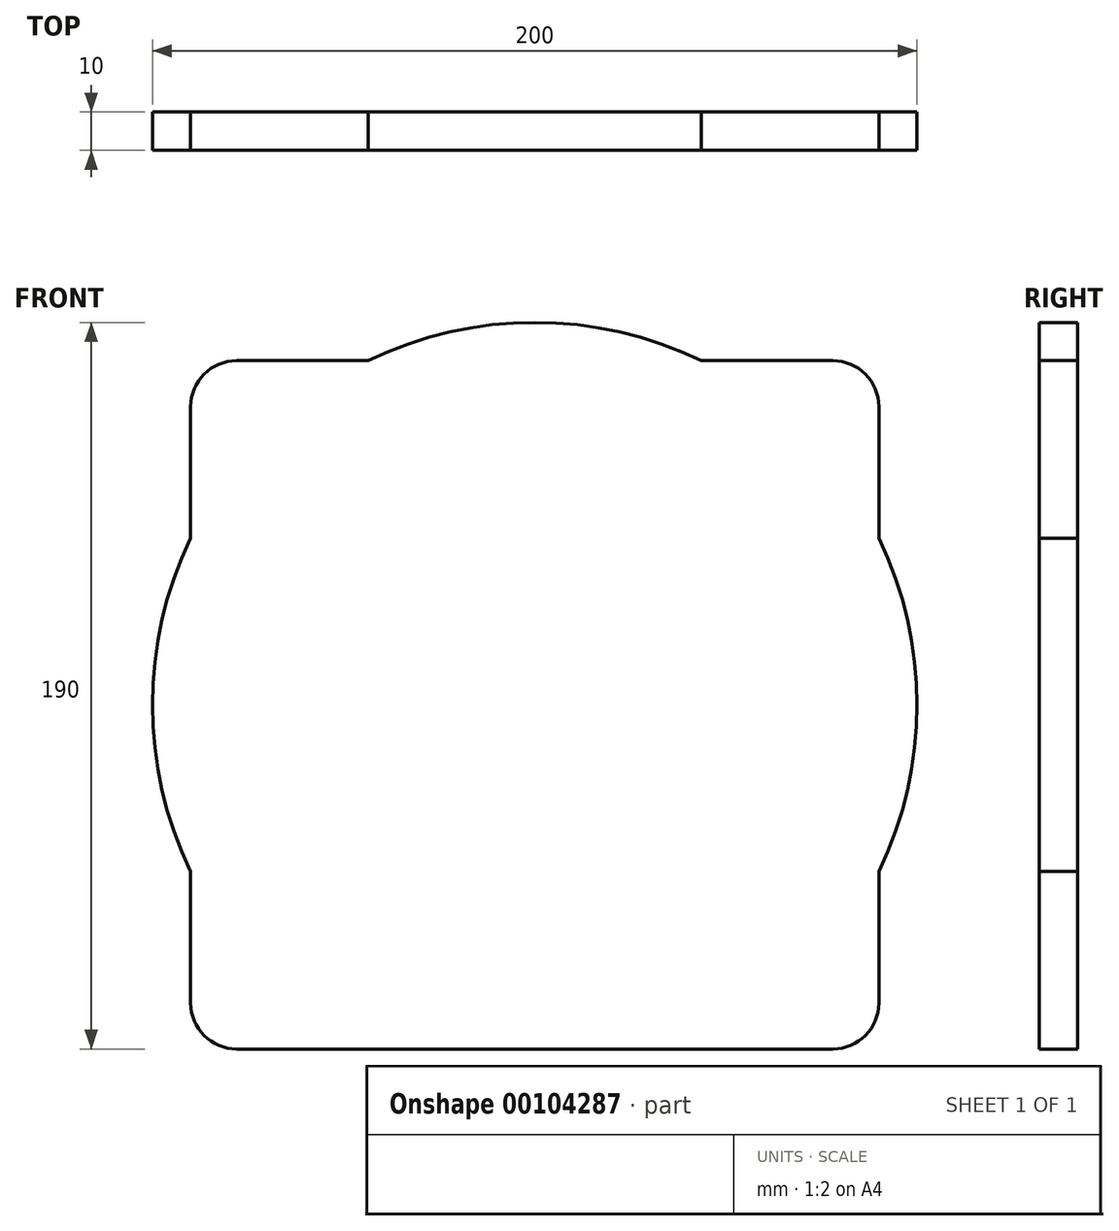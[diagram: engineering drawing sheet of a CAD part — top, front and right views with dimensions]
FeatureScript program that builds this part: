
annotation { "Feature Type Name" : "Feature", "Feature Type Description" : "" }
export const myFeature = defineFeature(function(context is Context, id is Id, definition is map)
    precondition{}
    {
        {
            var Q0;
            Q0=qCreatedBy(makeId("Front.planeOp"),FACE);
            var sketch = newSketch(context, id + "F0", { "sketchPlane" : qUnion([Q0])});
            skCircle(sketch, "E0", {"center": v(0, 0) * mm, "radius": 100 * mm});
            skLineSegment(sketch, "E1.bottom", {"start": v(78, 90) * mm, "end": v(-78, 90) * mm});
            skLineSegment(sketch, "E1.top", {"start": v(78, -90) * mm, "end": v(-78, -90) * mm});
            skLineSegment(sketch, "E1.left", {"start": v(90, 78) * mm, "end": v(90, -78) * mm});
            skLineSegment(sketch, "E1.right", {"start": v(-90, 78) * mm, "end": v(-90, -78) * mm});
            skPoint(sketch, "E2.visualSharp", {"position": v(-90, 90) * mm});
            skArc(sketch, "E2.filletArc", {"start": v(-78, 90) * mm, "mid": v(-86.49, 86.49) * mm, "end": v(-90, 78) * mm});
            skPoint(sketch, "E3.visualSharp", {"position": v(90, 90) * mm});
            skArc(sketch, "E3.filletArc", {"start": v(90, 78) * mm, "mid": v(86.49, 86.49) * mm, "end": v(78, 90) * mm});
            skPoint(sketch, "E4.visualSharp", {"position": v(90, -90) * mm});
            skArc(sketch, "E4.filletArc", {"start": v(78, -90) * mm, "mid": v(86.49, -86.49) * mm, "end": v(90, -78) * mm});
            skPoint(sketch, "E5.visualSharp", {"position": v(-90, -90) * mm});
            skArc(sketch, "E5.filletArc", {"start": v(-90, -78) * mm, "mid": v(-86.49, -86.49) * mm, "end": v(-78, -90) * mm});
            skSolve(sketch);
        }
        {
            var Q0;
            {var subQ5=sQuery(id+"F0.wireOp",EDGE,"E2.filletArc");Q0=makeQuery(id+"F0.imprint","IMPRINT",FACE,{"disambiguationData":[TD([[makeQuery(id+"F0.imprint","IMPRINT",EDGE,{"derivedFrom":subQ5}),1.0]])]});}
            var Q1;
            {var subQ0=sQuery(id+"F0.wireOp",EDGE,"E1.bottom");var subQ1=sQuery(id+"F0.wireOp",EDGE,"E0");var subQ2=makeQuery(id+"F0.imprint","INTERSECT",VERTEX,{"disambiguationData":[OD(0.0)],"derivedFrom":[subQ1,subQ0]});Q1=makeQuery(id+"F0.imprint","IMPRINT",FACE,{"disambiguationData":[TD([[makeQuery(id+"F0.imprint","IMPRINT",EDGE,{"disambiguationData":[TD([[subQ2,-1.0]])],"derivedFrom":subQ1}),1.0]])]});}
            var Q2;
            {var subQ5=sQuery(id+"F0.wireOp",EDGE,"E3.filletArc");Q2=makeQuery(id+"F0.imprint","IMPRINT",FACE,{"disambiguationData":[TD([[makeQuery(id+"F0.imprint","IMPRINT",EDGE,{"derivedFrom":subQ5}),1.0]])]});}
            var Q3;
            {var subQ5=sQuery(id+"F0.wireOp",EDGE,"E4.filletArc");Q3=makeQuery(id+"F0.imprint","IMPRINT",FACE,{"disambiguationData":[TD([[makeQuery(id+"F0.imprint","IMPRINT",EDGE,{"derivedFrom":subQ5}),1.0]])]});}
            var Q4;
            {var subQ5=sQuery(id+"F0.wireOp",EDGE,"E5.filletArc");Q4=makeQuery(id+"F0.imprint","IMPRINT",FACE,{"disambiguationData":[TD([[makeQuery(id+"F0.imprint","IMPRINT",EDGE,{"derivedFrom":subQ5}),1.0]])]});}
            var Q5;
            {var subQ1=sQuery(id+"F0.wireOp",EDGE,"E0");var subQ8=sQuery(id+"F0.wireOp",EDGE,"E1.bottom");var subQ11=makeQuery(id+"F0.imprint","INTERSECT",VERTEX,{"disambiguationData":[OD(0.0)],"derivedFrom":[subQ1,subQ8]});Q5=makeQuery(id+"F0.imprint","IMPRINT",FACE,{"disambiguationData":[TD([[makeQuery(id+"F0.imprint","IMPRINT",EDGE,{"disambiguationData":[TD([[subQ11,1.0]])],"derivedFrom":subQ1}),1.0]])]});}
            var Q6;
            {var subQ0=sQuery(id+"F0.wireOp",EDGE,"E1.right");var subQ1=sQuery(id+"F0.wireOp",EDGE,"E0");var subQ2=makeQuery(id+"F0.imprint","INTERSECT",VERTEX,{"disambiguationData":[OD(0.0)],"derivedFrom":[subQ1,subQ0]});Q6=makeQuery(id+"F0.imprint","IMPRINT",FACE,{"disambiguationData":[TD([[makeQuery(id+"F0.imprint","IMPRINT",EDGE,{"disambiguationData":[TD([[subQ2,-1.0]])],"derivedFrom":subQ1}),1.0]])]});}
            var Q7;
            {var subQ0=sQuery(id+"F0.wireOp",EDGE,"E1.top");var subQ1=sQuery(id+"F0.wireOp",EDGE,"E0");var subQ2=makeQuery(id+"F0.imprint","INTERSECT",VERTEX,{"disambiguationData":[OD(0.0)],"derivedFrom":[subQ1,subQ0]});Q7=makeQuery(id+"F0.imprint","IMPRINT",FACE,{"disambiguationData":[TD([[makeQuery(id+"F0.imprint","IMPRINT",EDGE,{"disambiguationData":[TD([[subQ2,-1.0]])],"derivedFrom":subQ1}),1.0]])]});}
            var Q8;
            {var subQ0=sQuery(id+"F0.wireOp",EDGE,"E1.left");var subQ1=sQuery(id+"F0.wireOp",EDGE,"E0");var subQ2=makeQuery(id+"F0.imprint","INTERSECT",VERTEX,{"disambiguationData":[OD(0.0)],"derivedFrom":[subQ1,subQ0]});Q8=makeQuery(id+"F0.imprint","IMPRINT",FACE,{"disambiguationData":[TD([[makeQuery(id+"F0.imprint","IMPRINT",EDGE,{"disambiguationData":[TD([[subQ2,1.0]])],"derivedFrom":subQ1}),1.0]])]});}
            extrude(context, id + "F1", {"entities" : qUnion([Q0, Q1, Q2, Q3, Q4, Q5, Q6, Q7, Q8]), "depth" : 10 * mm});
        }
    });
